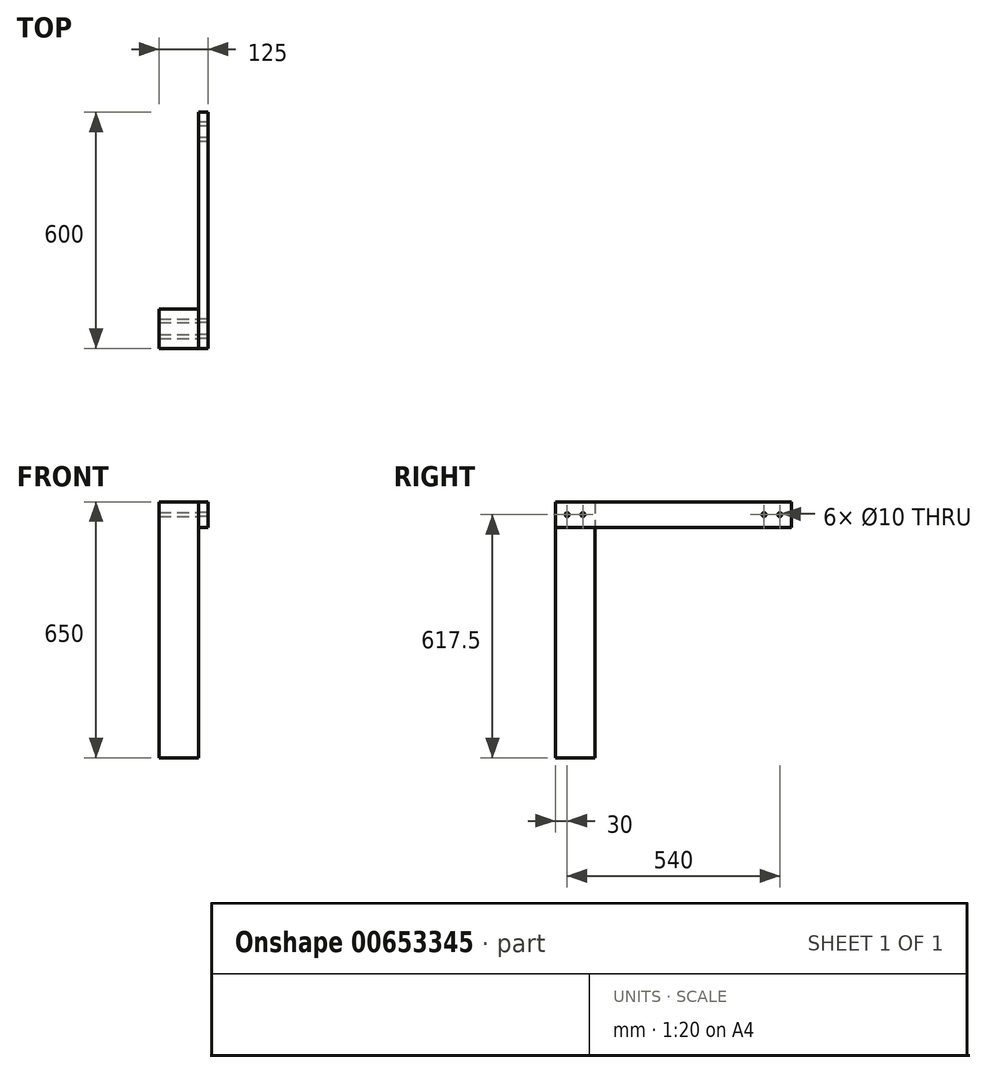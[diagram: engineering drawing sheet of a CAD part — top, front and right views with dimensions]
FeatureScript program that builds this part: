
annotation { "Feature Type Name" : "Feature", "Feature Type Description" : "" }
export const myFeature = defineFeature(function(context is Context, id is Id, definition is map)
    precondition{}
    {
        {
            var Q0;
            Q0=qCreatedBy(makeId("Top.planeOp"),FACE);
            var sketch = newSketch(context, id + "F0", { "sketchPlane" : qUnion([Q0])});
            skLineSegment(sketch, "E0.bottom", {"start": v(-100, -100) * mm, "end": v(0, -100) * mm});
            skLineSegment(sketch, "E0.top", {"start": v(-100, 0) * mm, "end": v(0, 0) * mm});
            skLineSegment(sketch, "E0.left", {"start": v(-100, -100) * mm, "end": v(-100, 0) * mm});
            skLineSegment(sketch, "E0.right", {"start": v(0, -100) * mm, "end": v(0, 0) * mm});
            skSolve(sketch);
        }
        {
            var Q0;
            Q0 = qSketchRegion(id + "F0", true);
            extrude(context, id + "F1", {"entities" : qUnion([Q0]), "depth" : 650 * mm, "offsetDistance" : 25 * mm});
        }
        {
            var Q0;
            Q0=makeQuery(id+"F1.opExtrude","SWEPT_FACE",FACE,{"disambiguationData":[OSD([sQuery(id+"F0.wireOp",EDGE,"E0.right")])]});
            var sketch = newSketch(context, id + "F2", { "sketchPlane" : qUnion([Q0])});
            skCircle(sketch, "E1", {"center": v(-70, 617.5) * mm, "radius": 5 * mm});
            skCircle(sketch, "E2", {"center": v(-30, 617.5) * mm, "radius": 5 * mm});
            skSolve(sketch);
        }
        {
            var Q0;
            Q0 = qSketchRegion(id + "F2", true);
            extrude(context, id + "F3", {"entities" : qUnion([Q0]), "operationType" : NewBodyOperationType.REMOVE, "endBound" : BoundingType.THROUGH_ALL, "oppositeDirection" : true, "depth" : 25 * mm, "offsetDistance" : 25 * mm});
        }
        {
            var Q0;
            Q0=qCreatedBy(makeId("Right.planeOp"),FACE);
            var sketch = newSketch(context, id + "F4", { "sketchPlane" : qUnion([Q0])});
            skLineSegment(sketch, "E3.bottom", {"start": v(-100, 650) * mm, "end": v(500, 650) * mm});
            skLineSegment(sketch, "E3.top", {"start": v(-100, 585) * mm, "end": v(500, 585) * mm});
            skLineSegment(sketch, "E3.left", {"start": v(-100, 650) * mm, "end": v(-100, 585) * mm});
            skLineSegment(sketch, "E3.right", {"start": v(500, 650) * mm, "end": v(500, 585) * mm});
            skCircle(sketch, "E4", {"center": v(-70, 617.5) * mm, "radius": 5 * mm});
            skCircle(sketch, "E5", {"center": v(-30, 617.5) * mm, "radius": 5 * mm});
            skLineSegment(sketch, "E6", {"start": v(200, 650) * mm, "end": v(200, 585) * mm, "construction": true});
            skCircle(sketch, "E7.MirrorC", {"center": v(470, 617.5) * mm, "radius": 5 * mm});
            skCircle(sketch, "E8.MirrorC", {"center": v(430, 617.5) * mm, "radius": 5 * mm});
            skSolve(sketch);
        }
        {
            var Q0;
            Q0=makeQuery(id+"F4.imprint","IMPRINT",FACE,{"disambiguationData":[TD([[makeQuery(id+"F4.imprint","IMPRINT",EDGE,{"derivedFrom":sQuery(id+"F4.wireOp",EDGE,"E3.bottom")}),-1.0]])]});
            extrude(context, id + "F5", {"entities" : qUnion([Q0]), "depth" : 25 * mm, "offsetDistance" : 25 * mm});
        }
    });
